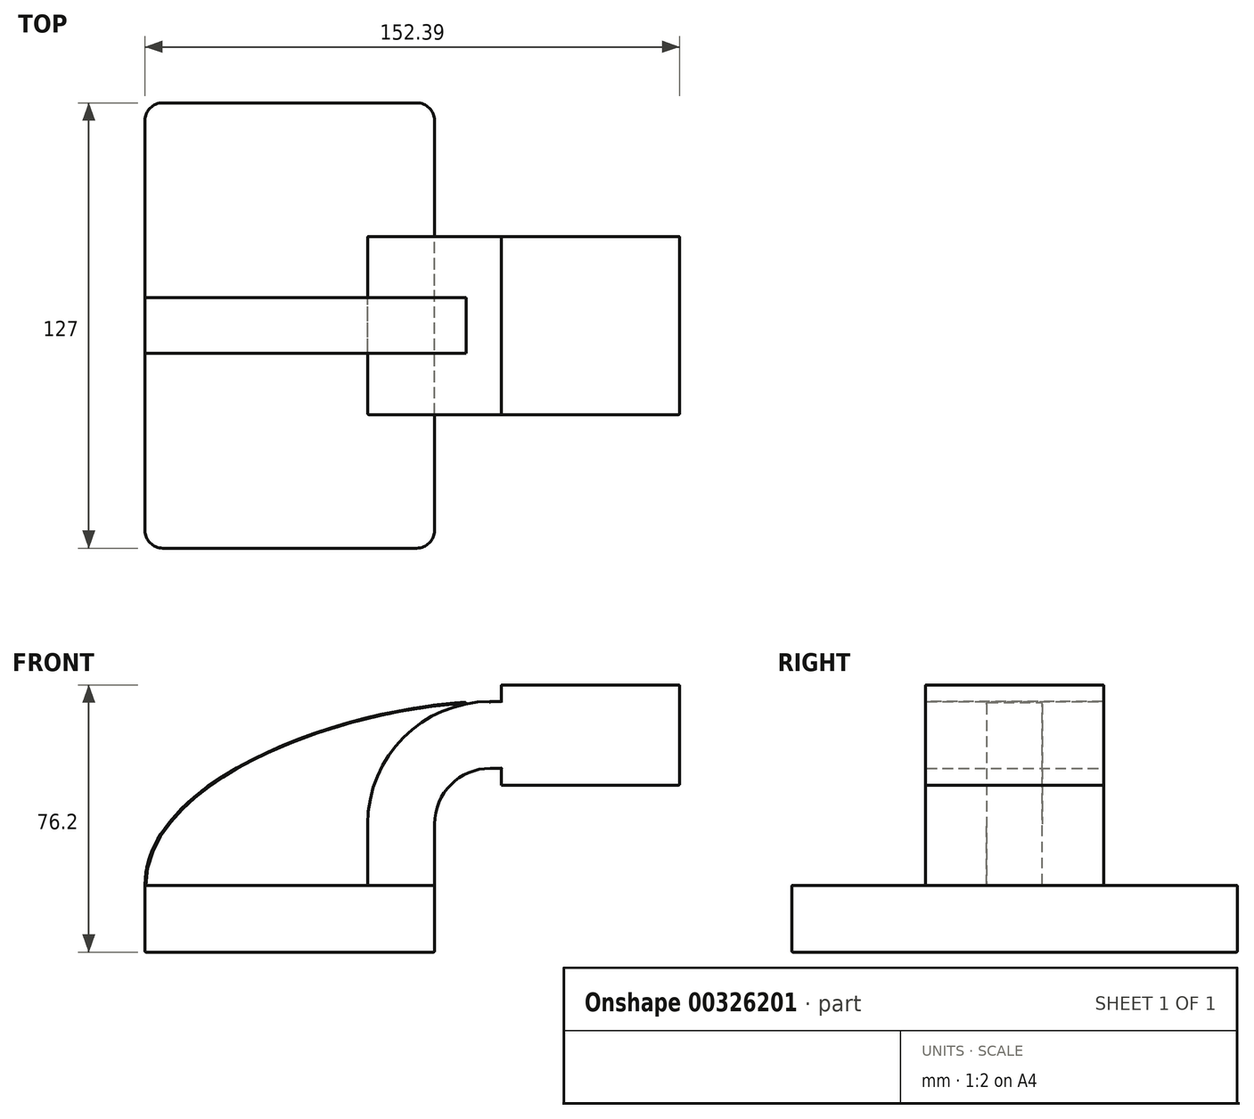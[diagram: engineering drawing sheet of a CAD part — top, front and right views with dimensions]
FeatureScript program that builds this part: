
annotation { "Feature Type Name" : "Feature", "Feature Type Description" : "" }
export const myFeature = defineFeature(function(context is Context, id is Id, definition is map)
    precondition{}
    {
        {
            var Q0;
            Q0=qCreatedBy(makeId("Front.planeOp"),FACE);
            var sketch = newSketch(context, id + "F0", { "sketchPlane" : qUnion([Q0])});
            skLineSegment(sketch, "E0.bottom", {"start": v(-41.28, -9.53) * mm, "end": v(41.28, -9.53) * mm});
            skLineSegment(sketch, "E0.top", {"start": v(-41.28, 9.52) * mm, "end": v(41.28, 9.52) * mm});
            skLineSegment(sketch, "E0.left", {"start": v(-41.28, -9.53) * mm, "end": v(-41.28, 9.52) * mm});
            skLineSegment(sketch, "E0.right", {"start": v(41.28, -9.53) * mm, "end": v(41.28, 9.52) * mm});
            skPoint(sketch, "E0.middle", {"position": v(0, 0) * mm});
            skLineSegment(sketch, "E1.bottom", {"start": v(111.12, 38.1) * mm, "end": v(60.32, 38.1) * mm});
            skLineSegment(sketch, "E1.top", {"start": v(111.12, 66.68) * mm, "end": v(60.32, 66.68) * mm});
            skLineSegment(sketch, "E1.left", {"start": v(111.12, 38.1) * mm, "end": v(111.12, 66.68) * mm});
            skLineSegment(sketch, "E1.right", {"start": v(60.32, 38.1) * mm, "end": v(60.32, 66.68) * mm});
            skPoint(sketch, "E1.middle", {"position": v(85.72, 52.39) * mm});
            skLineSegment(sketch, "E2", {"start": v(41.27, 9.52) * mm, "end": v(41.27, 27) * mm});
            skArc(sketch, "E3", {"start": v(41.27, 27) * mm, "mid": v(45.92, 38.23) * mm, "end": v(57.15, 42.88) * mm});
            skLineSegment(sketch, "E4", {"start": v(57.15, 42.88) * mm, "end": v(82.55, 42.88) * mm});
            skLineSegment(sketch, "E5.0", {"start": v(57.15, 61.93) * mm, "end": v(82.55, 61.93) * mm});
            skArc(sketch, "E5.1", {"start": v(22.22, 27) * mm, "mid": v(32.45, 51.7) * mm, "end": v(57.15, 61.93) * mm});
            skLineSegment(sketch, "E5.2", {"start": v(22.22, 9.52) * mm, "end": v(22.22, 27) * mm});
            skLineSegment(sketch, "E6", {"start": v(22.22, 9.52) * mm, "end": v(41.28, 9.52) * mm});
            skLineSegment(sketch, "E7", {"start": v(82.55, 61.93) * mm, "end": v(82.55, 42.88) * mm});
            skFitSpline(sketch, "E8", {"points": [v(-41.28, 9.53) * mm, v(57.15, 61.93) * mm], "startDerivative": vector(0.17, 93.35) * mm, "endDerivative": vector(117.01, 0.14) * mm});
            skSolve(sketch);
        }
        {
            var Q0;
            Q0=makeQuery(id+"F0.imprint","IMPRINT",FACE,{"disambiguationData":[TD([[makeQuery(id+"F0.imprint","IMPRINT",EDGE,{"derivedFrom":sQuery(id+"F0.wireOp",EDGE,"E2")}),1.0]])]});
            extrude(context, id + "F1", {"entities" : qUnion([Q0]), "depth" : 50.8 * mm, "symmetric" : true});
        }
        {
            var Q0;
            {var subQ5=sQuery(id+"F0.wireOp",EDGE,"E7");Q0=makeQuery(id+"F0.imprint","IMPRINT",FACE,{"disambiguationData":[TD([[makeQuery(id+"F0.imprint","IMPRINT",EDGE,{"derivedFrom":subQ5}),-1.0]])]});}
            var Q1;
            {var subQ1=sQuery(id+"F0.wireOp",EDGE,"E1.bottom");Q1=makeQuery(id+"F0.imprint","IMPRINT",FACE,{"disambiguationData":[TD([[makeQuery(id+"F0.imprint","IMPRINT",EDGE,{"derivedFrom":subQ1}),-1.0]])]});}
            extrude(context, id + "F2", {"entities" : qUnion([Q0, Q1]), "operationType" : NewBodyOperationType.ADD, "depth" : 50.8 * mm, "symmetric" : true});
        }
        {
            var Q0;
            Q0=makeQuery(id+"F0.imprint","IMPRINT",FACE,{"disambiguationData":[TD([[makeQuery(id+"F0.imprint","IMPRINT",EDGE,{"derivedFrom":sQuery(id+"F0.wireOp",EDGE,"E0.top")}),1.0]])]});
            extrude(context, id + "F3", {"entities" : qUnion([Q0]), "depth" : 15.88 * mm, "symmetric" : true});
        }
        {
            var Q0;
            Q0=makeQuery(id+"F0.imprint","IMPRINT",FACE,{"disambiguationData":[TD([[makeQuery(id+"F0.imprint","IMPRINT",EDGE,{"derivedFrom":sQuery(id+"F0.wireOp",EDGE,"E0.bottom")}),1.0]])]});
            extrude(context, id + "F4", {"entities" : qUnion([Q0]), "depth" : 127 * mm, "symmetric" : true});
        }
        {
            var Q0;
            Q0=makeQuery(id+"F4.opExtrude","CAP_EDGE",EDGE,{"disambiguationData":[OSD([sQuery(id+"F0.wireOp",EDGE,"E0.right")])],"isStart":false});
            var Q1;
            Q1=makeQuery(id+"F4.opExtrude","CAP_EDGE",EDGE,{"disambiguationData":[OSD([sQuery(id+"F0.wireOp",EDGE,"E0.left")])],"isStart":true});
            var Q2;
            Q2=makeQuery(id+"F4.opExtrude","CAP_EDGE",EDGE,{"disambiguationData":[OSD([sQuery(id+"F0.wireOp",EDGE,"E0.right")])],"isStart":true});
            var Q3;
            Q3=makeQuery(id+"F4.opExtrude","CAP_EDGE",EDGE,{"disambiguationData":[OSD([sQuery(id+"F0.wireOp",EDGE,"E0.left")])],"isStart":false});
            fillet(context, id + "F5", {"entities" : qUnion([Q0, Q1, Q2, Q3]), "radius" : 5.08 * mm, "tangentPropagation" : true, "allowEdgeOverflow" : false});
        }
        {
            var Q0;
            Q0=makeQuery(id+"F2.opExtrude","CAP_EDGE",EDGE,{"disambiguationData":[OSD([sQuery(id+"F0.wireOp",EDGE,"E1.top")])],"isStart":true});
            var Q1;
            Q1=makeQuery(id+"F2.opExtrude","CAP_EDGE",EDGE,{"disambiguationData":[OSD([sQuery(id+"F0.wireOp",EDGE,"E1.left")])],"isStart":true});
            var Q2;
            Q2=makeQuery(id+"F2.opExtrude","CAP_EDGE",EDGE,{"disambiguationData":[OSD([sQuery(id+"F0.wireOp",EDGE,"E1.bottom")])],"isStart":true});
            var Q3;
            Q3=makeQuery(id+"F2.opExtrude","SWEPT_EDGE",EDGE,{"disambiguationData":[OSD([sQuery(id+"F0.wireOp",EDGE,"E1.top"),sQuery(id+"F0.wireOp",EDGE,"E1.right")])]});
            var Q4;
            Q4=makeQuery(id+"F2.opExtrude","CAP_EDGE",EDGE,{"disambiguationData":[OSD([sQuery(id+"F0.wireOp",EDGE,"E1.top")])],"isStart":false});
            var Q5;
            Q5=makeQuery(id+"F1.opExtrude","CAP_EDGE",EDGE,{"disambiguationData":[OSD([sQuery(id+"F0.wireOp",EDGE,"E5.1")])],"isStart":true});
            var Q6;
            Q6=makeQuery(id+"F1.opExtrude","CAP_EDGE",EDGE,{"disambiguationData":[OSD([sQuery(id+"F0.wireOp",EDGE,"E5.2")])],"isStart":true});
            var Q7;
            Q7=makeQuery(id+"F1.opExtrude","CAP_EDGE",EDGE,{"disambiguationData":[OSD([sQuery(id+"F0.wireOp",EDGE,"E6")])],"isStart":true});
            var Q8;
            Q8=makeQuery(id+"F1.opExtrude","CAP_EDGE",EDGE,{"disambiguationData":[OSD([sQuery(id+"F0.wireOp",EDGE,"E3")])],"isStart":true});
            var Q9;
            Q9=makeQuery(id+"F1.opExtrude","CAP_EDGE",EDGE,{"disambiguationData":[OSD([sQuery(id+"F0.wireOp",EDGE,"E2")])],"isStart":true});
            var Q10;
            Q10=makeQuery(id+"F3.opExtrude","CAP_EDGE",EDGE,{"disambiguationData":[OSD([sQuery(id+"F0.wireOp",EDGE,"E0.top")])],"isStart":true});
            var Q11;
            Q11=makeQuery(id+"F4.opExtrude","CAP_EDGE",EDGE,{"disambiguationData":[OSD([sQuery(id+"F0.wireOp",EDGE,"E0.top"),sQuery(id+"F0.wireOp",EDGE,"E6")])],"isStart":true});
            var Q12;
            Q12=makeQuery(id+"F5.opFillet","BLEND_EDGE",EDGE,{"blendedFrom":[makeQuery(id+"F4.opExtrude","CAP_EDGE",EDGE,{"disambiguationData":[OSD([sQuery(id+"F0.wireOp",EDGE,"E0.right")])],"isStart":true}),makeQuery(id+"F4.opExtrude","SWEPT_FACE",FACE,{"disambiguationData":[OSD([sQuery(id+"F0.wireOp",EDGE,"E0.top"),sQuery(id+"F0.wireOp",EDGE,"E6")])]})],"blendedInto":[makeQuery(id+"F4.opExtrude","SWEPT_FACE",FACE,{"disambiguationData":[OSD([sQuery(id+"F0.wireOp",EDGE,"E0.top"),sQuery(id+"F0.wireOp",EDGE,"E6")])]})]});
            var Q13;
            Q13=makeQuery(id+"F4.opExtrude","SWEPT_EDGE",EDGE,{"disambiguationData":[OSD([sQuery(id+"F0.wireOp",EDGE,"E0.right"),sQuery(id+"F0.wireOp",EDGE,"E2"),sQuery(id+"F0.wireOp",EDGE,"E6")])]});
            var Q14;
            Q14=makeQuery(id+"F4.opExtrude","SWEPT_EDGE",EDGE,{"disambiguationData":[OSD([sQuery(id+"F0.wireOp",EDGE,"E0.top"),sQuery(id+"F0.wireOp",EDGE,"E0.left"),sQuery(id+"F0.wireOp",EDGE,"E8")])]});
            var Q15;
            Q15=makeQuery(id+"F3.opExtrude","CAP_EDGE",EDGE,{"disambiguationData":[OSD([sQuery(id+"F0.wireOp",EDGE,"E8")])],"isStart":true});
            var Q16;
            Q16=makeQuery(id+"F3.opExtrude","SWEPT_FACE",FACE,{"disambiguationData":[OSD([sQuery(id+"F0.wireOp",EDGE,"E8")])]});
            var Q17;
            Q17=makeQuery(id+"F1.opExtrude","CAP_EDGE",EDGE,{"disambiguationData":[OSD([sQuery(id+"F0.wireOp",EDGE,"E5.1")])],"isStart":false});
            var Q18;
            Q18=makeQuery(id+"F4.opExtrude","CAP_EDGE",EDGE,{"disambiguationData":[OSD([sQuery(id+"F0.wireOp",EDGE,"E0.top"),sQuery(id+"F0.wireOp",EDGE,"E6")])],"isStart":false});
            var Q19;
            Q19=makeQuery(id+"F4.opExtrude","SWEPT_EDGE",EDGE,{"disambiguationData":[OSD([sQuery(id+"F0.wireOp",EDGE,"E0.bottom"),sQuery(id+"F0.wireOp",EDGE,"E0.right")])]});
            var Q20;
            Q20=makeQuery(id+"F4.opExtrude","CAP_EDGE",EDGE,{"disambiguationData":[OSD([sQuery(id+"F0.wireOp",EDGE,"E0.bottom")])],"isStart":false});
            var Q21;
            Q21=makeQuery(id+"F4.opExtrude","CAP_FACE",FACE,{"disambiguationData":[OSD([sQuery(id+"F0.wireOp",EDGE,"E0.bottom"),sQuery(id+"F0.wireOp",EDGE,"E0.top"),sQuery(id+"F0.wireOp",EDGE,"E0.left"),sQuery(id+"F0.wireOp",EDGE,"E0.right"),sQuery(id+"F0.wireOp",EDGE,"E6")])],"isStart":false});
            var Q22;
            Q22=makeQuery(id+"F5.opFillet","BLEND_EDGE",EDGE,{"blendedFrom":[makeQuery(id+"F4.opExtrude","CAP_EDGE",EDGE,{"disambiguationData":[OSD([sQuery(id+"F0.wireOp",EDGE,"E0.left")])],"isStart":true}),makeQuery(id+"F4.opExtrude","SWEPT_FACE",FACE,{"disambiguationData":[OSD([sQuery(id+"F0.wireOp",EDGE,"E0.top"),sQuery(id+"F0.wireOp",EDGE,"E6")])]})],"blendedInto":[makeQuery(id+"F4.opExtrude","SWEPT_FACE",FACE,{"disambiguationData":[OSD([sQuery(id+"F0.wireOp",EDGE,"E0.top"),sQuery(id+"F0.wireOp",EDGE,"E6")])]})]});
            var Q23;
            Q23=makeQuery(id+"F2.opExtrude","CAP_EDGE",EDGE,{"disambiguationData":[OSD([sQuery(id+"F0.wireOp",EDGE,"E1.left")])],"isStart":false});
            var Q24;
            Q24=makeQuery(id+"F2.opExtrude","SWEPT_EDGE",EDGE,{"disambiguationData":[OSD([sQuery(id+"F0.wireOp",EDGE,"E1.top"),sQuery(id+"F0.wireOp",EDGE,"E1.left")])]});
            var Q25;
            Q25=makeQuery(id+"F2.opExtrude","SWEPT_EDGE",EDGE,{"disambiguationData":[OSD([sQuery(id+"F0.wireOp",EDGE,"E1.bottom"),sQuery(id+"F0.wireOp",EDGE,"E1.left")])]});
            var Q26;
            {var subQ0=sQuery(id+"F0.wireOp",EDGE,"E1.right");var subQ2=sQuery(id+"F0.wireOp",EDGE,"E4");Q26=makeQuery(id+"F2.boolean.opBoolean","SPLIT",EDGE,{"disambiguationData":[TD([makeQuery(id+"F1.opExtrude","SWEPT_FACE",FACE,{"disambiguationData":[OSD([subQ2])]})])],"derivedFrom":makeQuery(id+"F2.opExtrude","CAP_EDGE",EDGE,{"disambiguationData":[OSD([subQ0])],"isStart":false})});}
            var Q27;
            Q27=makeQuery(id+"F1.opExtrude","SWEPT_EDGE",EDGE,{"disambiguationData":[OSD([sQuery(id+"F0.wireOp",EDGE,"E2"),sQuery(id+"F0.wireOp",EDGE,"E3")])]});
            var Q28;
            Q28=makeQuery(id+"F1.opExtrude","CAP_EDGE",EDGE,{"disambiguationData":[OSD([sQuery(id+"F0.wireOp",EDGE,"E2")])],"isStart":false});
            var Q29;
            Q29=makeQuery(id+"F2.opExtrude","CAP_EDGE",EDGE,{"disambiguationData":[OSD([sQuery(id+"F0.wireOp",EDGE,"E1.bottom")])],"isStart":false});
            var Q30;
            Q30=makeQuery(id+"F1.opExtrude","CAP_EDGE",EDGE,{"disambiguationData":[OSD([sQuery(id+"F0.wireOp",EDGE,"E3")])],"isStart":false});
            fillet(context, id + "F6", {"entities" : qUnion([Q0, Q1, Q2, Q3, Q4, Q5, Q6, Q7, Q8, Q9, Q10, Q11, Q12, Q13, Q14, Q15, Q16, Q17, Q18, Q19, Q20, Q21, Q22, Q23, Q24, Q25, Q26, Q27, Q28, Q29, Q30]), "radius" : 0.25 * mm, "tangentPropagation" : true, "allowEdgeOverflow" : false});
        }
    });
